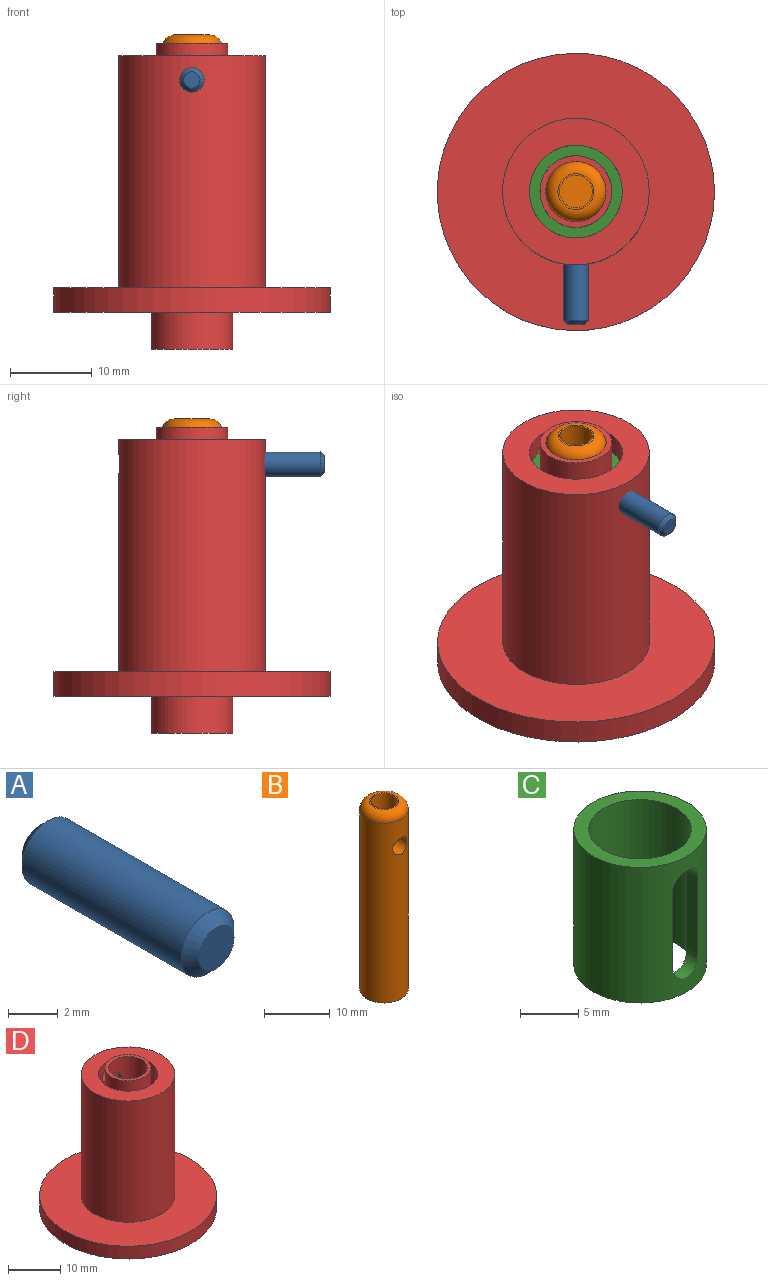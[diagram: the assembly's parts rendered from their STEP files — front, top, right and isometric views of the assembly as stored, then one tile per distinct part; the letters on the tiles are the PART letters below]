
ASSEMBLY  parts=4 mates=3
PART A: 5 faces, bbox 3x10x3 mm
  f0: cylinder r=1.5mm len=9mm, axis (0,1,0), area 84.8mm2, adj f3,f4
  f1: plane 2x2mm, normal (0,-1,0), area 3.1mm2, adj f3
  f2: plane 2x2mm, normal (0,1,0), area 3.1mm2, adj f4
  f3: cone r=1mm half-angle=45deg, axis (0,1,0), area 5.6mm2, adj f0,f1
  f4: cone r=1.5mm half-angle=45deg, axis (0,-1,0), area 5.6mm2, adj f0,f2
PART B: 7 faces, bbox 8x8x35 mm
  f0: cylinder r=3.7mm len=33.5mm, axis (0,0,-1), area 764.2mm2, adj f2,f3,f6
  f1: plane 4.4x4.4mm, normal (0,0,1), area 2.6mm2, adj f3,f4
  f2: plane 7.4x7.4mm, normal (0,0,-1), area 43mm2, adj f0
  f3: torus R=2.2mm, axis (0,0,1), area 46.7mm2, adj f0,f1
  f4: cylinder r=2mm len=4mm, axis (0,0,1), area 44mm2, adj f1,f5
  f5: plane 4x4mm, normal (0,0,1), area 12.6mm2, adj f4
  f6: cylinder r=1.51mm len=7.4mm, axis (0,1,0), area 67.1mm2, adj f0
PART C: 8 faces, bbox 11.4x11.4x14.3 mm
  f0: cylinder r=4.41mm len=14.25mm, axis (0,0,-1), area 362mm2, adj f2,f3,f4,f5,f6,f7
  f1: cylinder r=5.69mm len=14.25mm, axis (0,0,-1), area 477.3mm2, adj f2,f3,f4,f5,f6,f7
  f2: plane 11.39x11.39mm, normal (0,0,1), area 40.8mm2, adj f0,f1
  f3: plane 11.39x11.39mm, normal (0,0,-1), area 40.8mm2, adj f0,f1
  f4: plane 8.28x1.35mm, normal (-1,0,0), area 11.2mm2, adj f0,f1,f5,f7
  f5: cylinder r=1.51mm len=3.01mm, axis (0,1,0), area 6.1mm2, adj f0,f1,f4,f6
  f6: plane 8.41x1.35mm, normal (1,0,0), area 11.3mm2, adj f0,f1,f5,f7
  f7: cylinder r=1.51mm len=3.01mm, axis (0,1,0), area 6.1mm2, adj f0,f1,f4,f6
PART D: 15 faces, bbox 34x34x37.5 mm
  f0: cylinder r=17mm len=34mm, axis (0,0,-1), area 320.4mm2, adj f1,f2
  f1: plane 34x34mm, normal (0,0,1), area 653.5mm2, adj f0,f3
  f2: plane 34x34mm, normal (0,0,-1), area 829.4mm2, adj f0,f6
  f3: cylinder r=9mm len=28.5mm, axis (0,0,-1), area 1604.6mm2, adj f1,f4,f14
  f4: plane 18x18mm, normal (0,0,1), area 152.4mm2, adj f3,f8
  f5: plane 10x10mm, normal (0,0,-1), area 78.5mm2, adj f6
  f6: cylinder r=5mm len=10mm, axis (0,0,1), area 141.4mm2, adj f2,f5
  f7: plane 11.4x11.4mm, normal (0,0,1), area 41.2mm2, adj f8,f12
  f8: cylinder r=5.7mm len=28.5mm, axis (0,0,1), area 1013.6mm2, adj f4,f7,f14
  f9: plane 7.4x7.4mm, normal (0,0,1), area 43mm2, adj f10
  f10: cylinder r=3.7mm len=33mm, axis (0,0,1), area 760mm2, adj f9,f11,f13
  f11: plane 8.8x8.8mm, normal (0,0,1), area 17.8mm2, adj f10,f12
  f12: cylinder r=4.4mm len=30mm, axis (0,0,-1), area 822.2mm2, adj f7,f11,f13
  f13: cylinder r=1.5mm len=3mm, axis (0,-1,0), area 6.8mm2, adj f10,f12
  f14: cylinder r=1.5mm len=3.5mm, axis (0,-1,0), area 31.5mm2, adj f3,f8
PLACE A t=(-114.97,85.34,20.76)mm
PLACE B t=(-114.97,91.65,-8.72)mm
PLACE C rot(axis=(0,0,1),180deg) t=(-114.97,91.65,6.96)mm
PLACE D t=(-114.97,91.65,-7.74)mm
MATE cylindrical B.f0 <-> D.f10  axis (0,0,-1) through (-114.97,91.65,-8.72)mm
MATE cylindrical C.f0 <-> D.f8  axis (0,0,1) through (-114.97,91.65,21.21)mm
MATE cylindrical A.f0 <-> D.f13  axis (0,1,0) through (-114.97,80.34,20.76)mm
